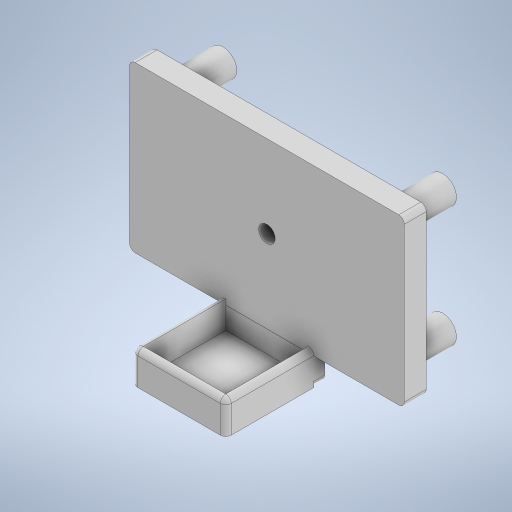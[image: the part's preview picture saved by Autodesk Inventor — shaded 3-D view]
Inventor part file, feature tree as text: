
AUTODESK INVENTOR PART (.ipt)
format: ipt  version: 2023 (Build 270158000, 158)  size: 338,432 bytes
history: native  units: in
note: dims shown in document units (in); Inventor stores cm internally (conversion verified against a paired STEP export)
features: sketch x9, extrude x7, fillet x5, hole x1
ambient origin geometry x8: Origin, YZ Plane, XZ Plane, XY Plane, X Axis, Y Axis, Z Axis, Center Point
bodies: Solid1 (feature_tree)
feature tree (22):
  extrude  "Extrusion1"  Depth=1.1811in
  fillet  "Fillet1"  Radius=0.1575in
  fillet  "Fillet2"  Radius=0.0394in
  hole  "Hole2"  [1 undecoded]
  sketch  "Sketch6"  dims[d20=0.1181in d21=0.2362in d22=0.1575in d23=0.0787in d24=90.0deg d25=0.315in d26=0.8108in d27=0.1969in d28=0.1969in]
  extrude  "Extrusion4"  Depth=0.1969in
  fillet  "Fillet3"  Radius=0.1969in
  extrude  "Extrusion5"  Depth=0.1969in
  extrude  "Extrusion6"  Depth=0.1969in
  extrude  "Extrusion8"  Depth=0.1969in
  extrude  "Extrusion9"  Depth=0.1575in
  fillet  "Fillet9"  Radius=0.1575in
  fillet  "Fillet10"  Radius=0.1575in
  sketch  "Sketch18"  dims[d56=0.0787in d57=0.0in d58=0.0394in d59=0.6693in d60=0.0394in d61=0.6299in d62=0.0in d63=0.0394in d64=0.1969in d65=0.0in d68=0.5906in d69=0.0394in d70=0.1969in d71=0.0in d76=0.0394in d77=0.1969in d78=0.0in d80=0.0394in d81=0.0394in d82=0.4724in d83=0.0in d7=0.0394in d8=0.0394in d9=0.0394in d10=0.0059in d11=0.0098in d12=0.0148in d13=0.5635in d14=0.0295in d15=0.8108in d16=0.0025in d17=0.0295in d18=0.0148in d31=0.0394in d32=0.0394in d33=0.0394in d34=0.0059in d35=0.0098in d36=0.0148in d37=0.5635in d73=0.0in d74=0.0in d75=0.0in d79=0.0344in d84=0.0394in d85=0.0059in d86=0.0098in d87=0.0148in d88=0.5635in d89=0.0295in d90=0.8108in d91=0.0025in d92=0.0295in d93=0.0148in]
  extrude  "Extrusion10"  Depth=0.1969in
  sketch  "Sketch1"  dims[d0=1.9685in d1=1.1811in d2=0.1575in d3=0.0in d4=0.0394in]
  sketch  "Sketch4"  dims[d5=0.0394in d19=0.1181in]
  sketch  "Sketch12"  dims[d29=0.1969in d30=0.1969in]
  sketch  "Sketch13"  dims[d38=0.1969in d39=0.1969in]
  sketch  "Sketch14"  dims[d40=0.1969in d41=0.1969in]
  sketch  "Sketch16"  dims[d42=0.1575in d43=0.1575in d44=0.1575in d45=0.1575in]
  sketch  "Sketch17"  dims[d53=0.6693in d55=0.1969in]
note: 1 required parameter value undecoded (feature->parameter linkage not recoverable at this tier; creation-order binding heuristic only, values carry confidence <= 0.55)
